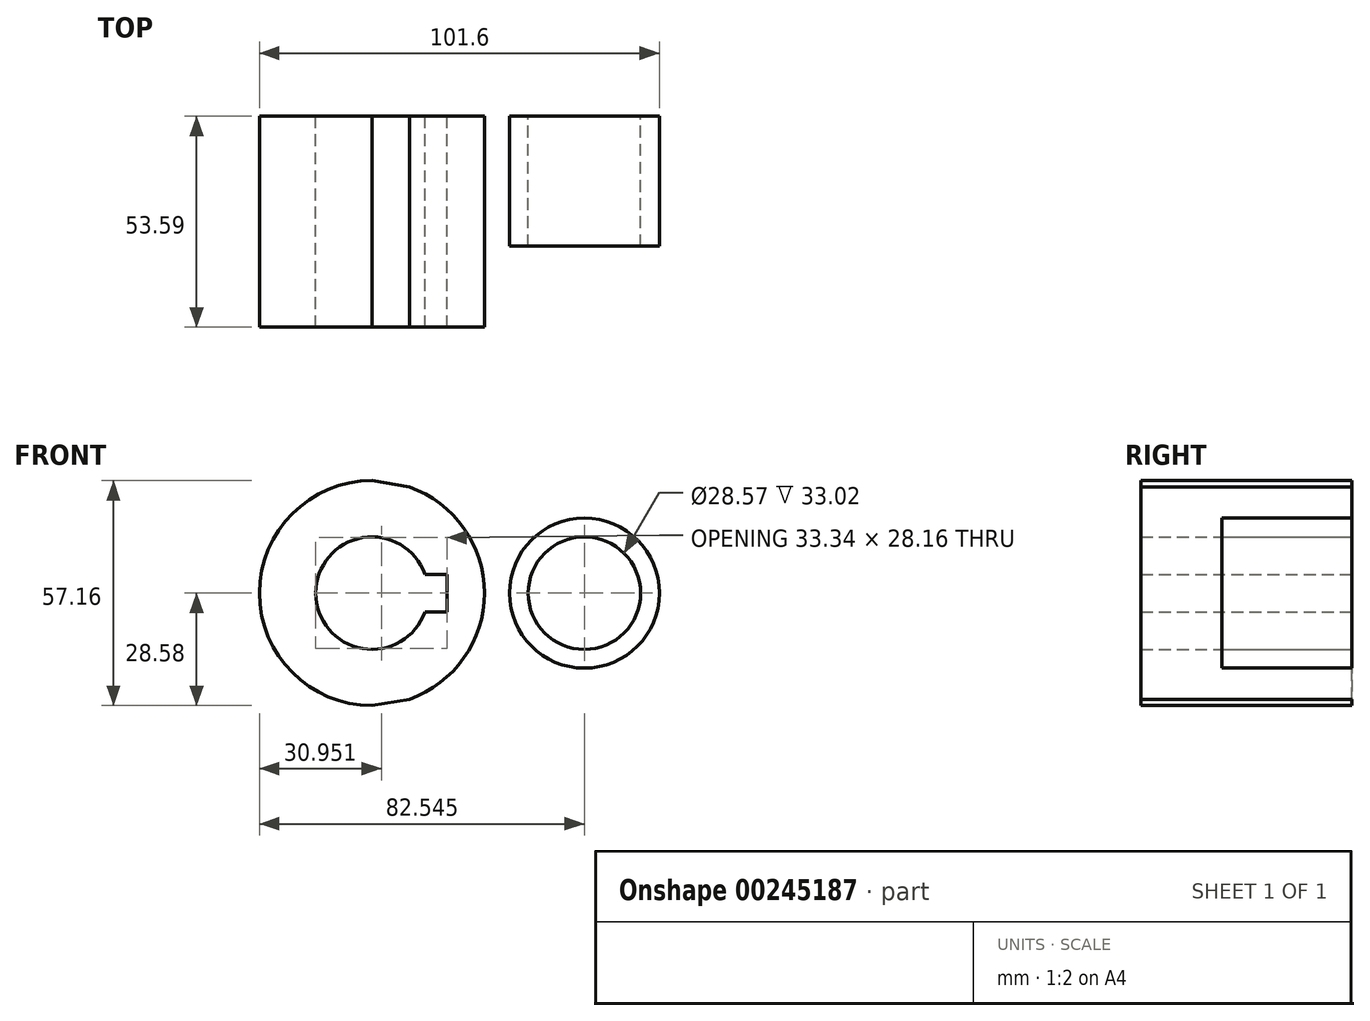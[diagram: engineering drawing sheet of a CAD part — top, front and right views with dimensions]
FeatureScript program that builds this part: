
annotation { "Feature Type Name" : "Feature", "Feature Type Description" : "" }
export const myFeature = defineFeature(function(context is Context, id is Id, definition is map)
    precondition{}
    {
        {
            var Q0;
            Q0=qCreatedBy(makeId("Front.planeOp"),FACE);
            var sketch = newSketch(context, id + "F0", { "sketchPlane" : qUnion([Q0])});
            skCircle(sketch, "E0", {"center": v(0, 0) * mm, "radius": 28.58 * mm});
            skCircle(sketch, "E1", {"center": v(53.98, 0) * mm, "radius": 19.05 * mm});
            skLineSegment(sketch, "E2", {"start": v(0, 28.58) * mm, "end": v(57.2, 18.78) * mm});
            skLineSegment(sketch, "E3", {"start": v(0, -28.58) * mm, "end": v(57.2, -18.78) * mm});
            skCircle(sketch, "E4", {"center": v(0, 0) * mm, "radius": 14.29 * mm});
            skCircle(sketch, "E5", {"center": v(53.98, 0) * mm, "radius": 14.29 * mm});
            skLineSegment(sketch, "E6.bottom", {"start": v(19.05, -4.76) * mm, "end": v(-19.05, -4.76) * mm});
            skLineSegment(sketch, "E6.top", {"start": v(19.05, 4.76) * mm, "end": v(-19.05, 4.76) * mm});
            skLineSegment(sketch, "E6.left", {"start": v(19.05, -4.76) * mm, "end": v(19.05, 4.76) * mm});
            skLineSegment(sketch, "E6.right", {"start": v(-19.05, -4.76) * mm, "end": v(-19.05, 4.76) * mm});
            skSolve(sketch);
        }
        {
            var Q0;
            {var subQ5=sQuery(id+"F0.wireOp",EDGE,"E6.right");Q0=makeQuery(id+"F0.imprint","IMPRINT",FACE,{"disambiguationData":[TD([[makeQuery(id+"F0.imprint","IMPRINT",EDGE,{"derivedFrom":subQ5}),-1.0]])]});}
            var Q1;
            {var subQ4=sQuery(id+"F0.wireOp",EDGE,"E6.left");Q1=makeQuery(id+"F0.imprint","IMPRINT",FACE,{"disambiguationData":[TD([[makeQuery(id+"F0.imprint","IMPRINT",EDGE,{"derivedFrom":subQ4}),-1.0]])]});}
            var Q2;
            {var subQ0=sQuery(id+"F0.wireOp",EDGE,"E2");var subQ1=sQuery(id+"F0.wireOp",EDGE,"E0");var subQ2=makeQuery(id+"F0.imprint","INTERSECT",VERTEX,{"disambiguationData":[OD(1.0)],"derivedFrom":[subQ1,subQ0]});Q2=makeQuery(id+"F0.imprint","IMPRINT",FACE,{"disambiguationData":[TD([[makeQuery(id+"F0.imprint","IMPRINT",EDGE,{"disambiguationData":[TD([[subQ2,1.0]])],"derivedFrom":subQ1}),-1.0]])]});}
            var Q3;
            Q3=makeQuery(id+"F0.imprint","IMPRINT",FACE,{"disambiguationData":[TD([[makeQuery(id+"F0.imprint","IMPRINT",EDGE,{"derivedFrom":sQuery(id+"F0.wireOp",EDGE,"E5")}),-1.0]])]});
            extrude(context, id + "F1", {"entities" : qUnion([Q0, Q1, Q2, Q3]), "depth" : 33.02 * mm});
        }
        {
            var Q0;
            {var subQ5=sQuery(id+"F0.wireOp",EDGE,"E6.right");Q0=makeQuery(id+"F0.imprint","IMPRINT",FACE,{"disambiguationData":[TD([[makeQuery(id+"F0.imprint","IMPRINT",EDGE,{"derivedFrom":subQ5}),-1.0]])]});}
            var Q1;
            {var subQ4=sQuery(id+"F0.wireOp",EDGE,"E6.left");Q1=makeQuery(id+"F0.imprint","IMPRINT",FACE,{"disambiguationData":[TD([[makeQuery(id+"F0.imprint","IMPRINT",EDGE,{"derivedFrom":subQ4}),-1.0]])]});}
            extrude(context, id + "F2", {"entities" : qUnion([Q0, Q1]), "operationType" : NewBodyOperationType.ADD, "depth" : 53.6 * mm});
        }
    });
